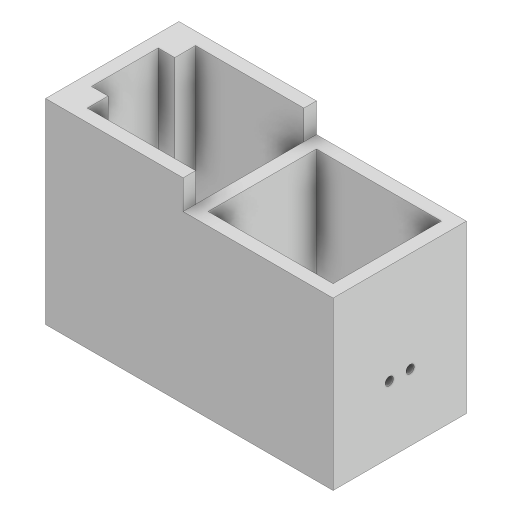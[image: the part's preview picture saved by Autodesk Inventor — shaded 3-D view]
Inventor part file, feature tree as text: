
AUTODESK INVENTOR PART (.ipt)
format: ipt  version: 2024.3 (Build 283343000, 343)  size: 404,480 bytes
history: native  units: mm
features: extrude x6, sketch x3, other x1
ambient origin geometry x8: Origin, YZ Plane, XZ Plane, XY Plane, X Axis, Y Axis, Z Axis, Center Point
bodies: Body1 (feature_tree)
feature tree (10):
  other  "Sólido1"
  extrude  "Extrusão1"  Depth=13.0mm
  extrude  "Extrusão2"  Depth=13.0mm
  sketch  "Esboço2"  dims[d0=13.0mm d1=13.0mm]
  extrude  "Extrusão3"  Depth=2.5mm
  sketch  "Esboço3"  dims[d2=15.0mm d3=13.0mm]
  extrude  "Extrusão4"  Depth=1.5mm
  extrude  "Extrusão5"  Depth=1.5mm
  extrude  "Extrusão8"  Depth=2.0mm
  sketch  "Esboço6"  dims[d4=8.0mm d5=2.5mm d6=1.5mm d7=1.5mm d8=2.0mm d9=1.5mm d10=1.5mm d11=1.5mm d12=1.5mm d13=0.0mm d14=20.0mm d15=0.0mm d23=8.0mm d24=10.0mm d25=0.0mm d26=1.0mm d27=1.0mm d28=8.0mm d29=8.0mm d30=1.25mm d31=1.25mm d38=10.0mm d39=0.0mm d40=1.0mm d42=6.5mm d44=10.0mm d45=0.0mm d66=16.5mm d67=0.0mm d68=3.5mm d69=0.0mm d78=3.0mm d79=3.0mm d80=3.0mm d81=3.0mm d41=0.872665mm d54=0.5mm d55=0.872665mm d56=0.5mm d57=0.872665mm d62=0.5mm d63=0.872665mm d64=0.5mm d65=0.872665mm]
